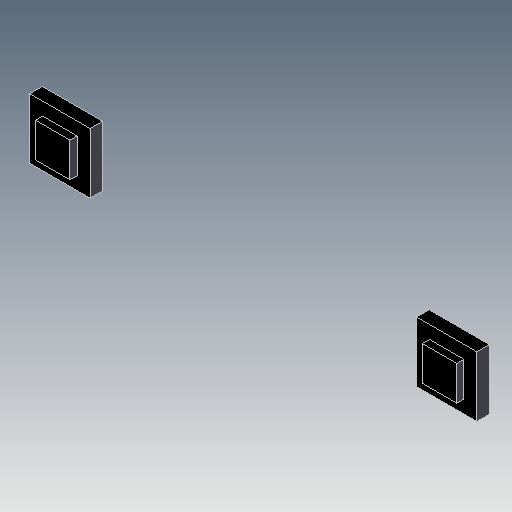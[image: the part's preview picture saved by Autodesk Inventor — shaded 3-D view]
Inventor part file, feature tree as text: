
AUTODESK INVENTOR PART (.ipt)
format: ipt  version: 2021 (Build 250183000, 183)  size: 171,520 bytes
history: native  units: mm
features: extrude x4, sketch x4
ambient origin geometry x8: Origin, YZ Plane, XZ Plane, XY Plane, X Axis, Y Axis, Z Axis, Center Point
bodies: Volumenkörper1 (feature_tree)
feature tree (8):
  extrude  "Extrusion1"  Depth=24.0mm
  extrude  "Extrusion2"  Depth=24.0mm
  extrude  "Extrusion3"  Depth=178.0mm
  extrude  "Extrusion4"  Depth=13.7mm
  sketch  "Skizze1"  dims[d0=178.0mm d1=24.0mm]
  sketch  "Skizze3"  dims[d2=24.0mm d3=24.0mm]
  sketch  "Skizze4"  dims[d4=5.0mm d5=0.0mm d10=178.0mm d11=24.0mm d12=24.0mm d13=24.0mm]
  sketch  "Skizze5"  dims[d14=13.7mm d15=13.7mm d16=2.85mm d17=0.0mm d18=178.0mm d19=24.0mm d20=24.0mm d21=24.0mm d22=14.0mm d23=14.0mm d24=3.0mm d25=0.0mm d26=24.0mm d27=24.0mm d28=0.0mm d29=0.0mm]
